# Revit family: Midas 15-27.5 Ton Cabinet Unit
name_source: partatom
category: Mechanical Equipment
revit_build: Autodesk Revit 2017 (Build: 20160225_1515(x64)
units: mm (PartAtom-declared; Revit-internal decimal feet)

## family parameters
Always vertical = No
Cut with Voids When Loaded = No
OmniClass Number = 23.75.00.00
OmniClass Title = Climate Control (HVAC)
Part Type = Normal
Room Calculation Point = No
Round Connector Dimension = Use Diameter
Shared = No
Work Plane-Based = Yes

## types (1)
- Cabinet Unit
    Altitude = 0"
    Ambient Air Temp = 0 °F
    Apparent load = 0 VA
    Back_Segment-1 = 27.34"
    Back_Segment-2 = 21.38"
    Base Height = 2.69"
    Base Material = Metal - JCI - Aluminum - Gray
    Brand = 1
    CTRL Alternate Condensate Drain_Back Offset = 9.63"
    CTRL Alternate Condensate Drain_Left Offset = 46.76"
    CTRL Chimney Top = 32.04"
    CTRL Drain_Bottom = 4.62"
    CTRL Drain_Left = 46.75"
    CTRL Elec. Entry Bottom = 6.46"
    CTRL Elec. Entry Top = 44.34"
    CTRL Fan 1 & 2_X-1 = 19.9"
    CTRL Fan 1_Y-1 = 21.41"
    CTRL Fan 2_Y-2 = 67.34"
    CTRL Fan 3 & 4_X-2 = 55.94"
    CTRL Fan 3_Y-3 = 27.41"
    CTRL Fan 4_Y-4 = 61.41"
    CTRL Gas Connection _Bottom = 18.87"
    CTRL Gas Connection_Left = 51.47"
    CTRL Inset Distance = 1.09"
    CTRL Space = 3.68"
    Cabinet Material = Metal - JCI - Tan
    Clearance Back = 72"
    Clearance Front = 84"
    Clearance Left = 60"
    Clearance Right = 60"
    Clearance Top = 120"
    Coil Material = Metal - JCI - Aluminum - Gray
    Compressor Guard Configuration = 1
    Compressor Guard_Sheet Metal = No
    Compressor Guard_Standard = Yes
    Condensate  Drain Diameter = 1"
    Condenser Fan Diameter = 30"
    Cooling & Heating Configuration = 1
    Curb Material = Metal - JCI - Aluminum - Gray
    Default Elevation = 48"
    Efficiency = Standard Efficiency
    Electric Heat TMBH = 0.0 Btu/h
    Electrical Entry Diameter = 0.22"
    Electrical Entry Diameter-OD = 0.32"
    Entering Air Temp DB = 0 °F
    Entering Air Temp WB = 0 °F
    Evaporator Drain Diameter-OD = 1.13"
    Exhaust Configuration = 1
    Exhaust Fan CFM = 0 CFM
    Exhaust Flue Opening Height = 3.74"
    Exhaust Flue Opening Width = 4.15"
    FLA = 0 A
    Frequency = 60 Hz
    Gas Connection Diameter = 0.75"
    Gas Connection Diameter-OD = 0.88"
    Gas Flow = 0 GPM
    Gas Heat MBH Input = 0.0 Btu/h
    Gas Heat MBH Output = 0.0 Btu/h
    Gas Heat Visibility = No
    Hail Guard = No
    Hail Guard Configuration = 0
    Hail Guard Visibility_1,2,3 = No
    Hail Guard Visibility_4,5,6 = No
    Hail Guard Visibility_7-10 = No
    Heating EAT = 0 °F
    Heating LAT = 0 °F
    MCA = 0 A
    MDEF/Max CB = 0 A
    MOP = 0 A
    Manufacturer = Johnson Controls, Inc.
    Model = York_AC_Package_(27.5_Ton)_Cooling Only
    Model Line Visibility_20 & 25 Ton = No
    Model Line Visibility_27.5 Ton = Yes
    Nominal Capacity Configuration = 5
    Nominal Cooling Capacity = 27.5 ton
    Number of Poles = 3
    OA Configuration = 3
    Power Factor = 1
    Refrigerant Used = R-410A
    Return Air Height = 68.00"
    Return Air Width = 19.25"
    Return Fan CFM = 0 CFM
    Return/Exhaust ESP = 0.00 in-wg
    SMBH Cooling = 0.0 ton
    Segment-1 = 5.85"
    Segment-2 = 19.66"
    Segment-3 = 14.64"
    Segment-4 = 11.68"
    Segment-5 = 24.71"
    Segment-6 = 8.05"
    Segment-7 = 19.05"
    Supply Air Height = 61.63"
    Supply Air Width = 25.50"
    Supply ESP = 0.00 in-wg
    Supply Fan CFM = 0 CFM
    Support Post = Yes
    TMBH Cooling = 0.0 ton
    Tonnage = 5
    URL = www.johnsoncontrols.com
    Unit Height = 57.22"
    Unit Leaving Air Temp DB = 0 °F
    Unit Leaving Air Temp WB = 0 °F
    Unit Length = 160.06"
    Unit Width = 88.75"
    Voltage = 230 V
    Weight = 0.00 lb

## geometry (parser evidence)
native form markers: Sweep x29
no freeform markers — native parametric forms only
